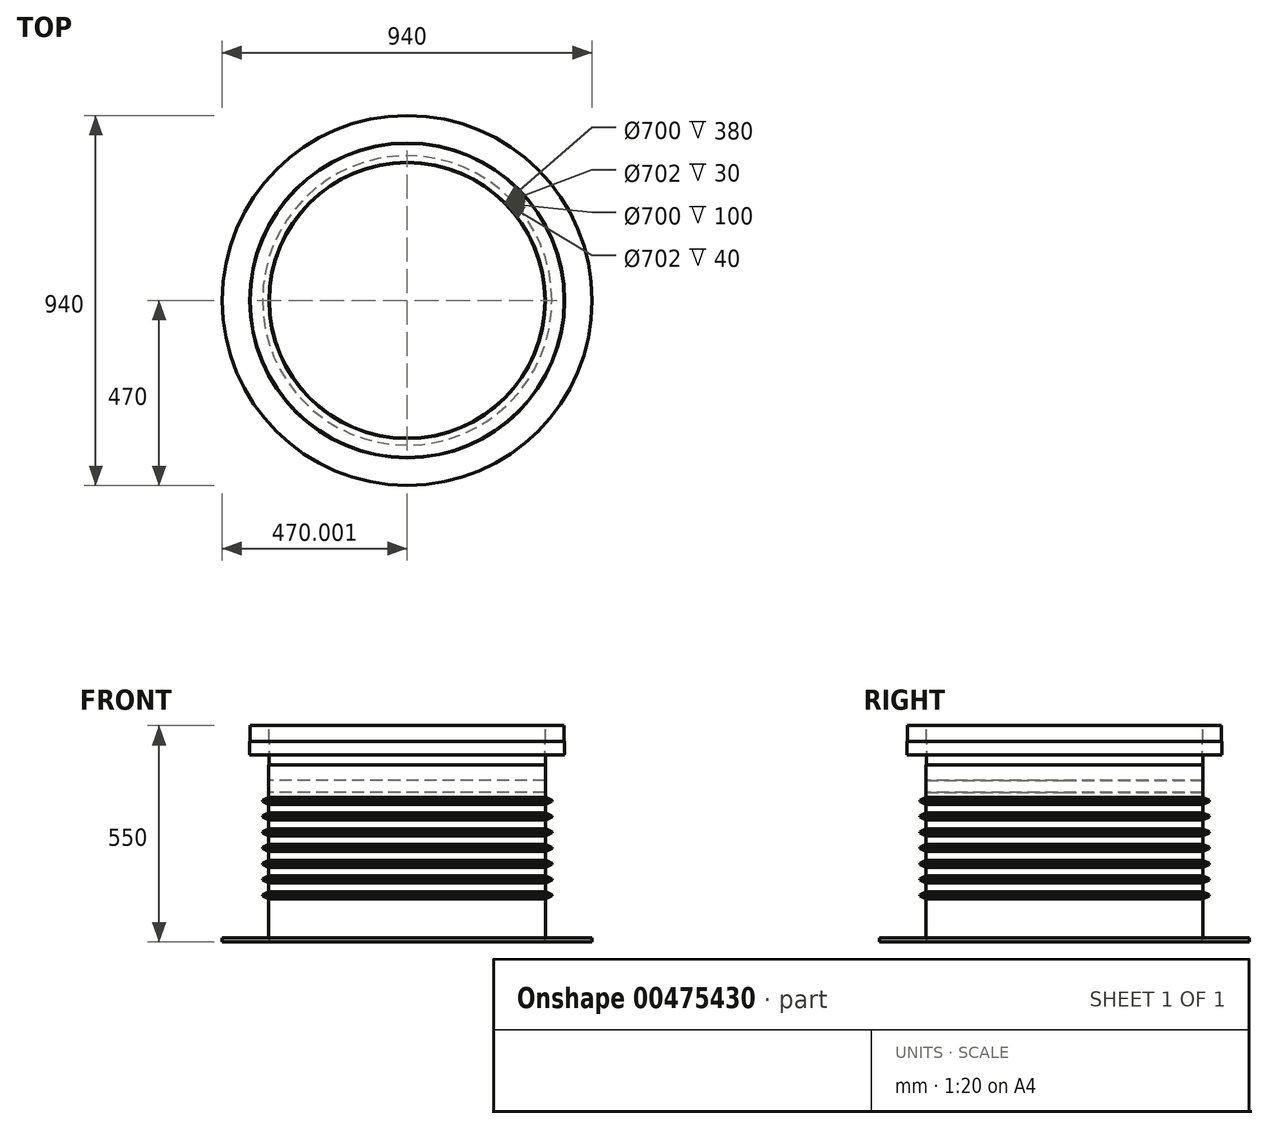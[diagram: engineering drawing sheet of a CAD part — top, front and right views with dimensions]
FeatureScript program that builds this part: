
annotation { "Feature Type Name" : "Feature", "Feature Type Description" : "" }
export const myFeature = defineFeature(function(context is Context, id is Id, definition is map)
    precondition{}
    {
        {
            var Q0;
            Q0=qCreatedBy(makeId("Front.planeOp"),FACE);
            var sketch = newSketch(context, id + "F0", { "sketchPlane" : qUnion([Q0])});
            skLineSegment(sketch, "E0", {"start": v(358.85, 550.1) * mm, "end": v(358.85, -1253.47) * mm, "construction": true});
            skLineSegment(sketch, "E1", {"start": v(8.85, -272.93) * mm, "end": v(8.85, 107.07) * mm});
            skLineSegment(sketch, "E2", {"start": v(7.85, 107.07) * mm, "end": v(7.85, -262.93) * mm});
            skLineSegment(sketch, "E3", {"start": v(7.85, -262.93) * mm, "end": v(-111.15, -262.93) * mm});
            skLineSegment(sketch, "E4", {"start": v(-111.15, -262.93) * mm, "end": v(-111.15, -272.93) * mm});
            skLineSegment(sketch, "E5", {"start": v(-111.15, -272.93) * mm, "end": v(8.85, -272.93) * mm});
            skLineSegment(sketch, "E6", {"start": v(8.85, 107.07) * mm, "end": v(7.85, 107.07) * mm});
            skLineSegment(sketch, "E7", {"start": v(6.85, -262.93) * mm, "end": v(6.85, -162.93) * mm});
            skLineSegment(sketch, "E8", {"start": v(6.85, -162.93) * mm, "end": v(-8.76, -155.65) * mm});
            skLineSegment(sketch, "E9", {"start": v(-8.76, -155.65) * mm, "end": v(-8.76, -152.65) * mm});
            skLineSegment(sketch, "E10", {"start": v(-8.76, -152.65) * mm, "end": v(6.85, -145.37) * mm});
            skLineSegment(sketch, "E11", {"start": v(6.85, -122.93) * mm, "end": v(6.85, -145.37) * mm});
            skLineSegment(sketch, "E12", {"start": v(7.85, -146) * mm, "end": v(-7.76, -153.29) * mm});
            skLineSegment(sketch, "E13", {"start": v(-7.76, -153.29) * mm, "end": v(-7.76, -155.01) * mm});
            skLineSegment(sketch, "E14", {"start": v(-7.76, -155.01) * mm, "end": v(7.85, -162.3) * mm});
            skLineSegment(sketch, "E15.0.1.0", {"start": v(7.85, -106) * mm, "end": v(-7.76, -113.29) * mm});
            skLineSegment(sketch, "E15.0.1.1", {"start": v(-8.76, -112.65) * mm, "end": v(6.85, -105.37) * mm});
            skLineSegment(sketch, "E15.0.1.2", {"start": v(6.85, -122.93) * mm, "end": v(-8.76, -115.65) * mm});
            skLineSegment(sketch, "E15.0.1.3", {"start": v(-8.76, -115.65) * mm, "end": v(-8.76, -112.65) * mm});
            skLineSegment(sketch, "E15.0.1.4", {"start": v(6.85, -82.93) * mm, "end": v(6.85, -105.37) * mm});
            skLineSegment(sketch, "E15.0.1.5", {"start": v(-7.76, -115.01) * mm, "end": v(7.85, -122.3) * mm});
            skLineSegment(sketch, "E15.0.1.6", {"start": v(-7.76, -113.29) * mm, "end": v(-7.76, -115.01) * mm});
            skLineSegment(sketch, "E15.0.2.0", {"start": v(7.85, -66) * mm, "end": v(-7.76, -73.29) * mm});
            skLineSegment(sketch, "E15.0.2.1", {"start": v(-8.76, -72.65) * mm, "end": v(6.85, -65.37) * mm});
            skLineSegment(sketch, "E15.0.2.2", {"start": v(6.85, -82.93) * mm, "end": v(-8.76, -75.65) * mm});
            skLineSegment(sketch, "E15.0.2.3", {"start": v(-8.76, -75.65) * mm, "end": v(-8.76, -72.65) * mm});
            skLineSegment(sketch, "E15.0.2.4", {"start": v(6.85, -42.93) * mm, "end": v(6.85, -65.37) * mm});
            skLineSegment(sketch, "E15.0.2.5", {"start": v(-7.76, -75.01) * mm, "end": v(7.85, -82.3) * mm});
            skLineSegment(sketch, "E15.0.2.6", {"start": v(-7.76, -73.29) * mm, "end": v(-7.76, -75.01) * mm});
            skLineSegment(sketch, "E15.0.3.0", {"start": v(7.85, -26) * mm, "end": v(-7.76, -33.29) * mm});
            skLineSegment(sketch, "E15.0.3.1", {"start": v(-8.76, -32.65) * mm, "end": v(6.85, -25.37) * mm});
            skLineSegment(sketch, "E15.0.3.2", {"start": v(6.85, -42.93) * mm, "end": v(-8.76, -35.65) * mm});
            skLineSegment(sketch, "E15.0.3.3", {"start": v(-8.76, -35.65) * mm, "end": v(-8.76, -32.65) * mm});
            skLineSegment(sketch, "E15.0.3.4", {"start": v(6.85, -2.93) * mm, "end": v(6.85, -25.37) * mm});
            skLineSegment(sketch, "E15.0.3.5", {"start": v(-7.76, -35.01) * mm, "end": v(7.85, -42.3) * mm});
            skLineSegment(sketch, "E15.0.3.6", {"start": v(-7.76, -33.29) * mm, "end": v(-7.76, -35.01) * mm});
            skLineSegment(sketch, "E15.0.4.0", {"start": v(7.85, 14) * mm, "end": v(-7.76, 6.71) * mm});
            skLineSegment(sketch, "E15.0.4.1", {"start": v(-8.76, 7.35) * mm, "end": v(6.85, 14.63) * mm});
            skLineSegment(sketch, "E15.0.4.2", {"start": v(6.85, -2.93) * mm, "end": v(-8.76, 4.35) * mm});
            skLineSegment(sketch, "E15.0.4.3", {"start": v(-8.76, 4.35) * mm, "end": v(-8.76, 7.35) * mm});
            skLineSegment(sketch, "E15.0.4.4", {"start": v(6.85, 37.07) * mm, "end": v(6.85, 14.63) * mm});
            skLineSegment(sketch, "E15.0.4.5", {"start": v(-7.76, 4.99) * mm, "end": v(7.85, -2.3) * mm});
            skLineSegment(sketch, "E15.0.4.6", {"start": v(-7.76, 6.71) * mm, "end": v(-7.76, 4.99) * mm});
            skLineSegment(sketch, "E15.0.5.0", {"start": v(7.85, 54) * mm, "end": v(-7.76, 46.71) * mm});
            skLineSegment(sketch, "E15.0.5.1", {"start": v(-8.76, 47.35) * mm, "end": v(6.85, 54.63) * mm});
            skLineSegment(sketch, "E15.0.5.2", {"start": v(6.85, 37.07) * mm, "end": v(-8.76, 44.35) * mm});
            skLineSegment(sketch, "E15.0.5.3", {"start": v(-8.76, 44.35) * mm, "end": v(-8.76, 47.35) * mm});
            skLineSegment(sketch, "E15.0.5.4", {"start": v(6.85, 77.07) * mm, "end": v(6.85, 54.63) * mm});
            skLineSegment(sketch, "E15.0.5.5", {"start": v(-7.76, 44.99) * mm, "end": v(7.85, 37.7) * mm});
            skLineSegment(sketch, "E15.0.5.6", {"start": v(-7.76, 46.71) * mm, "end": v(-7.76, 44.99) * mm});
            skLineSegment(sketch, "E15.0.6.0", {"start": v(7.85, 94) * mm, "end": v(-7.76, 86.71) * mm});
            skLineSegment(sketch, "E15.0.6.1", {"start": v(-8.76, 87.35) * mm, "end": v(6.85, 94.63) * mm});
            skLineSegment(sketch, "E15.0.6.2", {"start": v(6.85, 77.07) * mm, "end": v(-8.76, 84.35) * mm});
            skLineSegment(sketch, "E15.0.6.3", {"start": v(-8.76, 84.35) * mm, "end": v(-8.76, 87.35) * mm});
            skLineSegment(sketch, "E15.0.6.4", {"start": v(6.85, 117.07) * mm, "end": v(6.85, 94.63) * mm});
            skLineSegment(sketch, "E15.0.6.5", {"start": v(-7.76, 84.99) * mm, "end": v(7.85, 77.7) * mm});
            skLineSegment(sketch, "E15.0.6.6", {"start": v(-7.76, 86.71) * mm, "end": v(-7.76, 84.99) * mm});
            skLineSegment(sketch, "E15.direction1", {"start": v(-8.76, -155.65) * mm, "end": v(16.24, -155.65) * mm, "construction": true});
            skLineSegment(sketch, "E15.direction2", {"start": v(-8.76, -155.65) * mm, "end": v(-8.76, -115.65) * mm, "construction": true});
            skLineSegment(sketch, "E16", {"start": v(6.85, 117.07) * mm, "end": v(6.85, 177.07) * mm});
            skLineSegment(sketch, "E17", {"start": v(7.85, 107.07) * mm, "end": v(7.85, 177.07) * mm});
            skLineSegment(sketch, "E18", {"start": v(8.85, 137.07) * mm, "end": v(8.85, 237.07) * mm});
            skLineSegment(sketch, "E19", {"start": v(8.85, 237.07) * mm, "end": v(7.85, 237.07) * mm});
            skLineSegment(sketch, "E20", {"start": v(7.85, 237.07) * mm, "end": v(7.85, 277.07) * mm});
            skLineSegment(sketch, "E21", {"start": v(7.85, 277.07) * mm, "end": v(-40.15, 277.07) * mm});
            skLineSegment(sketch, "E22", {"start": v(-40.15, 277.07) * mm, "end": v(-40.15, 237.07) * mm});
            skLineSegment(sketch, "E23", {"start": v(-40.15, 237.07) * mm, "end": v(-41.15, 237.07) * mm});
            skLineSegment(sketch, "E24", {"start": v(-41.15, 237.07) * mm, "end": v(-41.15, 202.07) * mm});
            skLineSegment(sketch, "E25", {"start": v(-41.15, 202.07) * mm, "end": v(7.85, 202.07) * mm});
            skLineSegment(sketch, "E26", {"start": v(7.85, 202.07) * mm, "end": v(7.85, 137.07) * mm});
            skLineSegment(sketch, "E27", {"start": v(6.85, 177.07) * mm, "end": v(7.85, 177.07) * mm});
            skLineSegment(sketch, "E28", {"start": v(7.85, 137.07) * mm, "end": v(8.85, 137.07) * mm});
            skSolve(sketch);
        }
        {
            var Q0;
            Q0=makeQuery(id+"F0.imprint","IMPRINT",FACE,{"disambiguationData":[TD([[makeQuery(id+"F0.imprint","IMPRINT",EDGE,{"derivedFrom":sQuery(id+"F0.wireOp",EDGE,"E1")}),1.0]])]});
            var Q1;
            {var subQ6=sQuery(id+"F0.wireOp",EDGE,"E7");Q1=makeQuery(id+"F0.imprint","IMPRINT",FACE,{"disambiguationData":[TD([[makeQuery(id+"F0.imprint","IMPRINT",EDGE,{"derivedFrom":subQ6}),-1.0]])]});}
            var Q2;
            Q2=makeQuery(id+"F0.imprint","IMPRINT",FACE,{"disambiguationData":[TD([[makeQuery(id+"F0.imprint","IMPRINT",EDGE,{"derivedFrom":sQuery(id+"F0.wireOp",EDGE,"E18")}),1.0]])]});
            var Q3;
            {var subQ0=sQuery(id+"F0.wireOp",EDGE,"E15.0.6.0");Q3=makeQuery(id+"F0.imprint","IMPRINT",FACE,{"disambiguationData":[TD([[makeQuery(id+"F0.imprint","IMPRINT",EDGE,{"derivedFrom":subQ0}),1.0]])]});}
            var Q4;
            {var subQ0=sQuery(id+"F0.wireOp",EDGE,"E15.0.5.0");Q4=makeQuery(id+"F0.imprint","IMPRINT",FACE,{"disambiguationData":[TD([[makeQuery(id+"F0.imprint","IMPRINT",EDGE,{"derivedFrom":subQ0}),1.0]])]});}
            var Q5;
            {var subQ0=sQuery(id+"F0.wireOp",EDGE,"E15.0.4.0");Q5=makeQuery(id+"F0.imprint","IMPRINT",FACE,{"disambiguationData":[TD([[makeQuery(id+"F0.imprint","IMPRINT",EDGE,{"derivedFrom":subQ0}),1.0]])]});}
            var Q6;
            {var subQ0=sQuery(id+"F0.wireOp",EDGE,"E15.0.3.0");Q6=makeQuery(id+"F0.imprint","IMPRINT",FACE,{"disambiguationData":[TD([[makeQuery(id+"F0.imprint","IMPRINT",EDGE,{"derivedFrom":subQ0}),1.0]])]});}
            var Q7;
            {var subQ0=sQuery(id+"F0.wireOp",EDGE,"E15.0.2.0");Q7=makeQuery(id+"F0.imprint","IMPRINT",FACE,{"disambiguationData":[TD([[makeQuery(id+"F0.imprint","IMPRINT",EDGE,{"derivedFrom":subQ0}),1.0]])]});}
            var Q8;
            {var subQ0=sQuery(id+"F0.wireOp",EDGE,"E15.0.1.0");Q8=makeQuery(id+"F0.imprint","IMPRINT",FACE,{"disambiguationData":[TD([[makeQuery(id+"F0.imprint","IMPRINT",EDGE,{"derivedFrom":subQ0}),1.0]])]});}
            var Q9;
            {var subQ0=sQuery(id+"F0.wireOp",EDGE,"E12");Q9=makeQuery(id+"F0.imprint","IMPRINT",FACE,{"disambiguationData":[TD([[makeQuery(id+"F0.imprint","IMPRINT",EDGE,{"derivedFrom":subQ0}),1.0]])]});}
            var Q10;
            Q10=sQuery(id+"F0.wireOp",EDGE,"E0");
            revolve(context, id + "F1", {"entities" : qUnion([Q0, Q1, Q2, Q3, Q4, Q5, Q6, Q7, Q8, Q9]), "axis" : qUnion([Q10]), "revolveType" : RevolveType.FULL});
        }
    });
